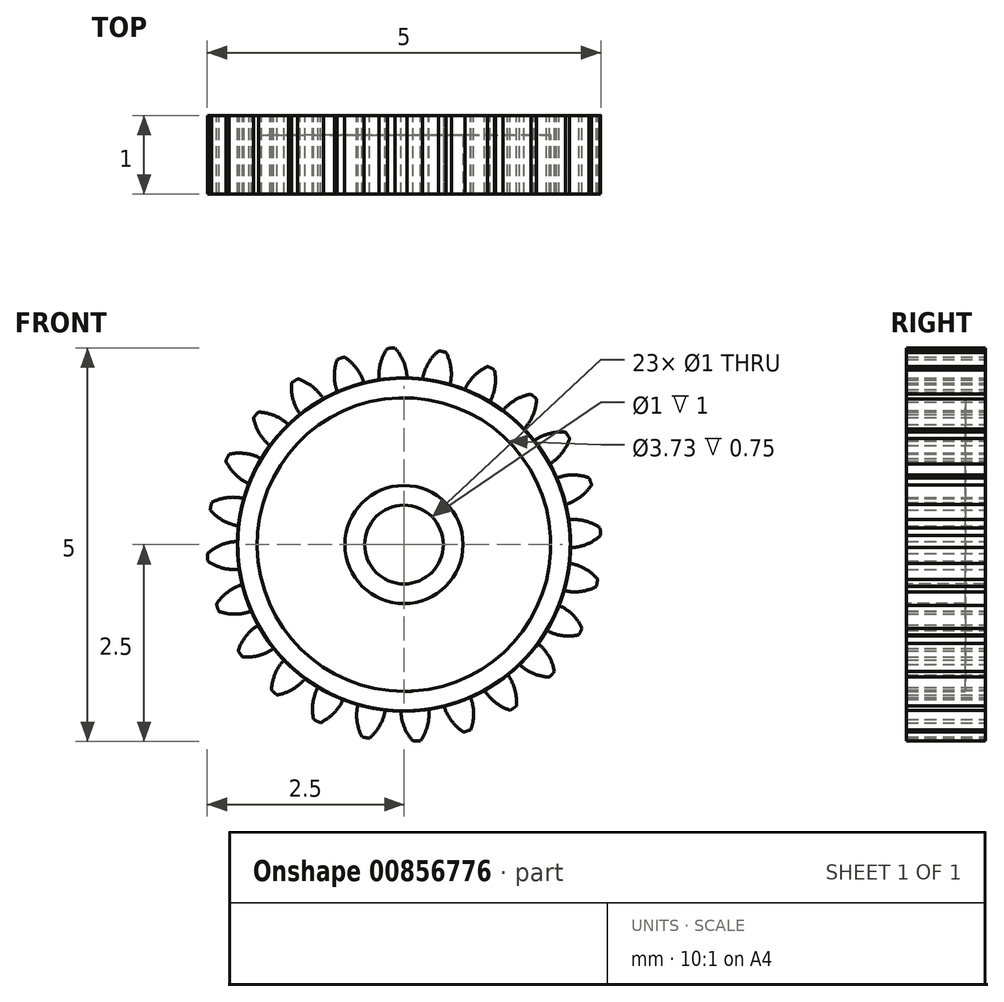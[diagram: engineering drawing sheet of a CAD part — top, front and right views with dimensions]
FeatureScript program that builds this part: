
annotation { "Feature Type Name" : "Feature", "Feature Type Description" : "" }
export const myFeature = defineFeature(function(context is Context, id is Id, definition is map)
    precondition{}
    {
        {
            var Q0;
            Q0=qCreatedBy(makeId("Front.planeOp"),FACE);
            var sketch = newSketch(context, id + "F0", { "sketchPlane" : qUnion([Q0])});
            skCircle(sketch, "E0", {"center": v(0, 0) * mm, "radius": 2.12 * mm});
            skCircle(sketch, "E1", {"center": v(0, 0) * mm, "radius": 2.31 * mm, "construction": true});
            skCircle(sketch, "E2", {"center": v(0, 0) * mm, "radius": 2.5 * mm, "construction": true});
            skLineSegment(sketch, "E3", {"start": v(0, 0) * mm, "end": v(0, 4.46) * mm, "construction": true});
            skLineSegment(sketch, "E4", {"start": v(0, 0) * mm, "end": v(-0.3, 4.55) * mm, "construction": true});
            skLineSegment(sketch, "E5", {"start": v(0, 2.31) * mm, "end": v(-4.04, 2.31) * mm, "construction": true});
            skLineSegment(sketch, "E6", {"start": v(0, 2.31) * mm, "end": v(-4.1, 0.82) * mm, "construction": true});
            skCircle(sketch, "E7", {"center": v(0, 2.31) * mm, "radius": 0.57 * mm, "construction": true});
            skCircle(sketch, "E8", {"center": v(0, 0) * mm, "radius": 2.17 * mm, "construction": true});
            skCircle(sketch, "E9", {"center": v(-0.54, 2.1) * mm, "radius": 0.57 * mm, "construction": true});
            skArc(sketch, "E10", {"start": v(0, 2.31) * mm, "mid": v(-0.05, 2.4) * mm, "end": v(-0.12, 2.5) * mm});
            skArc(sketch, "E11", {"start": v(0.04, 2.11) * mm, "mid": v(0.03, 2.21) * mm, "end": v(0, 2.31) * mm});
            skArc(sketch, "E12.MirrorCS", {"start": v(-0.3, 2.3) * mm, "mid": v(-0.27, 2.4) * mm, "end": v(-0.21, 2.5) * mm});
            skArc(sketch, "E13.MirrorCS", {"start": v(-0.31, 2.1) * mm, "mid": v(-0.32, 2.2) * mm, "end": v(-0.3, 2.3) * mm});
            skArc(sketch, "E14", {"start": v(-0.12, 2.5) * mm, "mid": v(-0.16, 2.5) * mm, "end": v(-0.21, 2.5) * mm});
            skSolve(sketch);
        }
        {
            var Q0;
            {var subQ0=sQuery(id+"F0.wireOp",EDGE,"E0");var subQ1=makeQuery(id+"F0.imprint","INTERSECT",VERTEX,{"derivedFrom":[subQ0,sQuery(id+"F0.wireOp",EDGE,"E11")]});Q0=makeQuery(id+"F0.imprint","IMPRINT",FACE,{"disambiguationData":[TD([[makeQuery(id+"F0.imprint","IMPRINT",EDGE,{"disambiguationData":[TD([[subQ1,-1.0]])],"derivedFrom":subQ0}),1.0]])]});}
            var Q1;
            Q1=makeQuery(id+"F0.imprint","IMPRINT",FACE,{"disambiguationData":[TD([[makeQuery(id+"F0.imprint","IMPRINT",EDGE,{"derivedFrom":sQuery(id+"F0.wireOp",EDGE,"E10")}),1.0]])]});
            extrude(context, id + "F1", {"entities" : qUnion([Q0, Q1]), "depth" : 1 * mm, "offsetDistance" : 25 * mm});
        }
        {
            var Q0;
            Q0=makeQuery(id+"F1.opExtrude","SWEPT_BODY",BODY,{"disambiguationData":[OSD([sQuery(id+"F0.wireOp",EDGE,"E0"),sQuery(id+"F0.wireOp",EDGE,"E10"),sQuery(id+"F0.wireOp",EDGE,"E11"),sQuery(id+"F0.wireOp",EDGE,"E12.MirrorCS"),sQuery(id+"F0.wireOp",EDGE,"E13.MirrorCS"),sQuery(id+"F0.wireOp",EDGE,"E14")])]});
            var Q1;
            Q1=makeQuery(id+"F1.opExtrude","SWEPT_FACE",FACE,{"disambiguationData":[OSD([sQuery(id+"F0.wireOp",EDGE,"E0")])]});
            circularPattern(context, id + "F2", {"entities" : qUnion([Q0]), "axis" : qUnion([Q1]), "angle" : 360 * degree, "instanceCount" : 24, "equalSpace" : true});
        }
        {
            var Q0;
            Q0=makeQuery(id+"F1.opExtrude","CAP_FACE",FACE,{"disambiguationData":[OSD([sQuery(id+"F0.wireOp",EDGE,"E0"),sQuery(id+"F0.wireOp",EDGE,"E10"),sQuery(id+"F0.wireOp",EDGE,"E11"),sQuery(id+"F0.wireOp",EDGE,"E12.MirrorCS"),sQuery(id+"F0.wireOp",EDGE,"E13.MirrorCS"),sQuery(id+"F0.wireOp",EDGE,"E14")])],"isStart":false});
            cPlane(context, id + "F3", {"entities" : qUnion([Q0]), "cplaneType" : CPlaneType.OFFSET, "offset" : 0 * mm, "width" : 150 * mm, "height" : 150 * mm});
        }
        {
            var Q0;
            Q0=qCreatedBy(id+"F3.planeOp",FACE);
            var sketch = newSketch(context, id + "F4", { "sketchPlane" : qUnion([Q0])});
            skCircle(sketch, "E15", {"center": v(0, 0) * mm, "radius": 0.5 * mm});
            skSolve(sketch);
        }
        {
            var Q0;
            Q0=makeQuery(id+"F4.imprint","IMPRINT",FACE,{"disambiguationData":[TD([[makeQuery(id+"F4.imprint","IMPRINT",EDGE,{"derivedFrom":sQuery(id+"F4.wireOp",EDGE,"E15")}),1.0]])]});
            extrude(context, id + "F5", {"entities" : qUnion([Q0]), "operationType" : NewBodyOperationType.REMOVE, "endBound" : BoundingType.THROUGH_ALL, "oppositeDirection" : true, "depth" : 25 * mm, "offsetDistance" : 25 * mm});
        }
        {
            var Q0;
            Q0=makeQuery(id+"F1.opExtrude","CAP_FACE",FACE,{"disambiguationData":[OSD([sQuery(id+"F0.wireOp",EDGE,"E0"),sQuery(id+"F0.wireOp",EDGE,"E10"),sQuery(id+"F0.wireOp",EDGE,"E11"),sQuery(id+"F0.wireOp",EDGE,"E12.MirrorCS"),sQuery(id+"F0.wireOp",EDGE,"E13.MirrorCS"),sQuery(id+"F0.wireOp",EDGE,"E14")])],"isStart":false});
            shell(context, id + "F6", {"entities" : qUnion([Q0]), "thickness" : 0.25 * mm});
        }
    });
